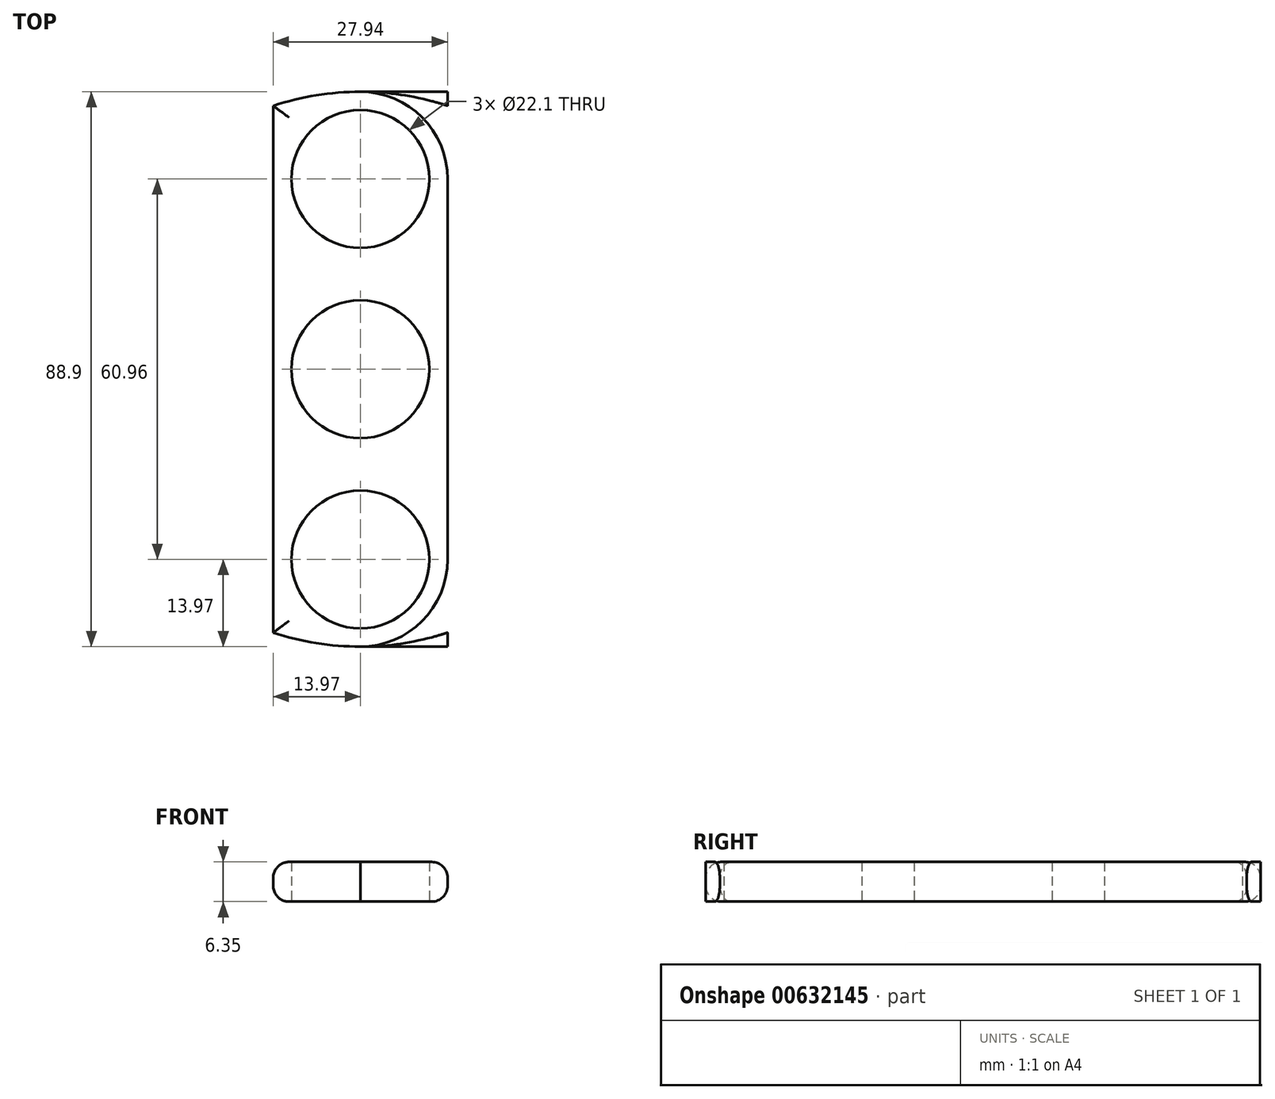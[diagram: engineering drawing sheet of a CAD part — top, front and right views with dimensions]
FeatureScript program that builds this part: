
annotation { "Feature Type Name" : "Feature", "Feature Type Description" : "" }
export const myFeature = defineFeature(function(context is Context, id is Id, definition is map)
    precondition{}
    {
        {
            var Q0;
            Q0=qCreatedBy(makeId("Top.planeOp"),FACE);
            var sketch = newSketch(context, id + "F0", { "sketchPlane" : qUnion([Q0])});
            skCircle(sketch, "E0", {"center": v(0, 0) * mm, "radius": 44.45 * mm});
            skCircle(sketch, "E1", {"center": v(0, 0) * mm, "radius": 11.05 * mm});
            skLineSegment(sketch, "E2", {"start": v(0, 0) * mm, "end": v(0, 30.48) * mm});
            skCircle(sketch, "E3", {"center": v(0, 30.48) * mm, "radius": 11.05 * mm});
            skLineSegment(sketch, "E4", {"start": v(0, 0) * mm, "end": v(0, -30.48) * mm});
            skCircle(sketch, "E5", {"center": v(0, -30.48) * mm, "radius": 11.05 * mm});
            skCircle(sketch, "E6", {"center": v(0, 30.48) * mm, "radius": 13.97 * mm});
            skCircle(sketch, "E7", {"center": v(0, 0) * mm, "radius": 13.97 * mm});
            skCircle(sketch, "E8", {"center": v(0, -30.48) * mm, "radius": 13.97 * mm});
            skLineSegment(sketch, "E9", {"start": v(0, 30.48) * mm, "end": v(0, 44.45) * mm});
            skLineSegment(sketch, "E10", {"start": v(0, 44.45) * mm, "end": v(13.97, 44.45) * mm});
            skLineSegment(sketch, "E11", {"start": v(13.97, 44.45) * mm, "end": v(-13.97, 44.45) * mm});
            skPoint(sketch, "E11.endSnap0", {"position": v(6.99, 44.45) * mm});
            skLineSegment(sketch, "E12", {"start": v(0, -30.48) * mm, "end": v(0, -44.45) * mm});
            skLineSegment(sketch, "E13", {"start": v(0, -44.45) * mm, "end": v(-13.97, -44.45) * mm});
            skLineSegment(sketch, "E14", {"start": v(-13.97, -44.45) * mm, "end": v(13.97, -44.45) * mm});
            skLineSegment(sketch, "E15", {"start": v(13.97, -44.45) * mm, "end": v(13.97, 44.45) * mm});
            skLineSegment(sketch, "E16", {"start": v(-13.97, 44.45) * mm, "end": v(-13.97, -44.45) * mm});
            skSolve(sketch);
        }
        {
            var Q0;
            {var subQ1=sQuery(id+"F0.wireOp",EDGE,"E0");var subQ3=sQuery(id+"F0.wireOp",EDGE,"E16");var subQ4=makeQuery(id+"F0.imprint","INTERSECT",VERTEX,{"disambiguationData":[OD(0.0)],"derivedFrom":[subQ1,subQ3]});Q0=makeQuery(id+"F0.imprint","IMPRINT",FACE,{"disambiguationData":[TD([[makeQuery(id+"F0.imprint","IMPRINT",EDGE,{"disambiguationData":[TD([[subQ4,-1.0]])],"derivedFrom":subQ3}),1.0]])]});}
            var Q1;
            {var subQ1=sQuery(id+"F0.wireOp",EDGE,"E0");var subQ3=sQuery(id+"F0.wireOp",EDGE,"E15");var subQ4=makeQuery(id+"F0.imprint","INTERSECT",VERTEX,{"disambiguationData":[OD(0.0)],"derivedFrom":[subQ1,subQ3]});Q1=makeQuery(id+"F0.imprint","IMPRINT",FACE,{"disambiguationData":[TD([[makeQuery(id+"F0.imprint","IMPRINT",EDGE,{"disambiguationData":[TD([[subQ4,1.0]])],"derivedFrom":subQ3}),1.0]])]});}
            var Q2;
            {var subQ0=sQuery(id+"F0.wireOp",EDGE,"E6");var subQ1=sQuery(id+"F0.wireOp",EDGE,"E2");var subQ2=makeQuery(id+"F0.imprint","INTERSECT",VERTEX,{"derivedFrom":[subQ1,subQ0]});Q2=makeQuery(id+"F0.imprint","IMPRINT",FACE,{"disambiguationData":[TD([[makeQuery(id+"F0.imprint","IMPRINT",EDGE,{"disambiguationData":[TD([[subQ2,-1.0]])],"derivedFrom":subQ1}),-1.0]])]});}
            var Q3;
            {var subQ0=sQuery(id+"F0.wireOp",EDGE,"E6");var subQ1=sQuery(id+"F0.wireOp",EDGE,"E2");var subQ2=makeQuery(id+"F0.imprint","INTERSECT",VERTEX,{"derivedFrom":[subQ1,subQ0]});Q3=makeQuery(id+"F0.imprint","IMPRINT",FACE,{"disambiguationData":[TD([[makeQuery(id+"F0.imprint","IMPRINT",EDGE,{"disambiguationData":[TD([[subQ2,-1.0]])],"derivedFrom":subQ1}),1.0]])]});}
            var Q4;
            {var subQ0=sQuery(id+"F0.wireOp",EDGE,"E7");var subQ1=sQuery(id+"F0.wireOp",EDGE,"E2");var subQ2=makeQuery(id+"F0.imprint","INTERSECT",VERTEX,{"derivedFrom":[subQ1,subQ0]});Q4=makeQuery(id+"F0.imprint","IMPRINT",FACE,{"disambiguationData":[TD([[makeQuery(id+"F0.imprint","IMPRINT",EDGE,{"disambiguationData":[TD([[subQ2,-1.0]])],"derivedFrom":subQ1}),1.0]])]});}
            var Q5;
            {var subQ0=sQuery(id+"F0.wireOp",EDGE,"E7");var subQ1=sQuery(id+"F0.wireOp",EDGE,"E2");var subQ2=makeQuery(id+"F0.imprint","INTERSECT",VERTEX,{"derivedFrom":[subQ1,subQ0]});Q5=makeQuery(id+"F0.imprint","IMPRINT",FACE,{"disambiguationData":[TD([[makeQuery(id+"F0.imprint","IMPRINT",EDGE,{"disambiguationData":[TD([[subQ2,-1.0]])],"derivedFrom":subQ1}),-1.0]])]});}
            var Q6;
            {var subQ1=sQuery(id+"F0.wireOp",EDGE,"E2");var subQ5=sQuery(id+"F0.wireOp",EDGE,"E1");var subQ8=makeQuery(id+"F0.imprint","INTERSECT",VERTEX,{"derivedFrom":[subQ5,subQ1]});Q6=makeQuery(id+"F0.imprint","IMPRINT",FACE,{"disambiguationData":[TD([[makeQuery(id+"F0.imprint","IMPRINT",EDGE,{"disambiguationData":[TD([[subQ8,-1.0]])],"derivedFrom":subQ5}),-1.0]])]});}
            var Q7;
            {var subQ1=sQuery(id+"F0.wireOp",EDGE,"E2");var subQ5=sQuery(id+"F0.wireOp",EDGE,"E1");var subQ8=makeQuery(id+"F0.imprint","INTERSECT",VERTEX,{"derivedFrom":[subQ5,subQ1]});Q7=makeQuery(id+"F0.imprint","IMPRINT",FACE,{"disambiguationData":[TD([[makeQuery(id+"F0.imprint","IMPRINT",EDGE,{"disambiguationData":[TD([[subQ8,1.0]])],"derivedFrom":subQ5}),-1.0]])]});}
            var Q8;
            {var subQ0=sQuery(id+"F0.wireOp",EDGE,"E7");var subQ1=sQuery(id+"F0.wireOp",EDGE,"E4");var subQ2=makeQuery(id+"F0.imprint","INTERSECT",VERTEX,{"derivedFrom":[subQ1,subQ0]});Q8=makeQuery(id+"F0.imprint","IMPRINT",FACE,{"disambiguationData":[TD([[makeQuery(id+"F0.imprint","IMPRINT",EDGE,{"disambiguationData":[TD([[subQ2,-1.0]])],"derivedFrom":subQ1}),-1.0]])]});}
            var Q9;
            {var subQ0=sQuery(id+"F0.wireOp",EDGE,"E7");var subQ1=sQuery(id+"F0.wireOp",EDGE,"E4");var subQ2=makeQuery(id+"F0.imprint","INTERSECT",VERTEX,{"derivedFrom":[subQ1,subQ0]});Q9=makeQuery(id+"F0.imprint","IMPRINT",FACE,{"disambiguationData":[TD([[makeQuery(id+"F0.imprint","IMPRINT",EDGE,{"disambiguationData":[TD([[subQ2,-1.0]])],"derivedFrom":subQ1}),1.0]])]});}
            var Q10;
            {var subQ0=sQuery(id+"F0.wireOp",EDGE,"E8");var subQ1=sQuery(id+"F0.wireOp",EDGE,"E4");var subQ2=makeQuery(id+"F0.imprint","INTERSECT",VERTEX,{"derivedFrom":[subQ1,subQ0]});Q10=makeQuery(id+"F0.imprint","IMPRINT",FACE,{"disambiguationData":[TD([[makeQuery(id+"F0.imprint","IMPRINT",EDGE,{"disambiguationData":[TD([[subQ2,-1.0]])],"derivedFrom":subQ1}),1.0]])]});}
            var Q11;
            {var subQ1=sQuery(id+"F0.wireOp",EDGE,"E8");var subQ4=sQuery(id+"F0.wireOp",EDGE,"E4");var subQ5=makeQuery(id+"F0.imprint","INTERSECT",VERTEX,{"derivedFrom":[subQ4,subQ1]});Q11=makeQuery(id+"F0.imprint","IMPRINT",FACE,{"disambiguationData":[TD([[makeQuery(id+"F0.imprint","IMPRINT",EDGE,{"disambiguationData":[TD([[subQ5,-1.0]])],"derivedFrom":subQ4}),-1.0]])]});}
            var Q12;
            {var subQ1=sQuery(id+"F0.wireOp",EDGE,"E0");var subQ3=sQuery(id+"F0.wireOp",EDGE,"E16");var subQ4=makeQuery(id+"F0.imprint","INTERSECT",VERTEX,{"disambiguationData":[OD(1.0)],"derivedFrom":[subQ1,subQ3]});Q12=makeQuery(id+"F0.imprint","IMPRINT",FACE,{"disambiguationData":[TD([[makeQuery(id+"F0.imprint","IMPRINT",EDGE,{"disambiguationData":[TD([[subQ4,1.0]])],"derivedFrom":subQ3}),1.0]])]});}
            var Q13;
            {var subQ1=sQuery(id+"F0.wireOp",EDGE,"E0");var subQ3=sQuery(id+"F0.wireOp",EDGE,"E15");var subQ4=makeQuery(id+"F0.imprint","INTERSECT",VERTEX,{"disambiguationData":[OD(1.0)],"derivedFrom":[subQ1,subQ3]});Q13=makeQuery(id+"F0.imprint","IMPRINT",FACE,{"disambiguationData":[TD([[makeQuery(id+"F0.imprint","IMPRINT",EDGE,{"disambiguationData":[TD([[subQ4,-1.0]])],"derivedFrom":subQ3}),1.0]])]});}
            extrude(context, id + "F1", {"entities" : qUnion([Q0, Q1, Q2, Q3, Q4, Q5, Q6, Q7, Q8, Q9, Q10, Q11, Q12, Q13]), "depth" : 6.35 * mm, "offsetDistance" : 25.4 * mm});
        }
        {
            var Q0;
            {var subQ0=sQuery(id+"F0.wireOp",EDGE,"E0");Q0=makeQuery(id+"F1.opExtrude","CAP_EDGE",EDGE,{"disambiguationData":[OSD([subQ0]),TDD([makeQuery(id+"F0.imprint","IMPRINT",EDGE,{"disambiguationData":[TD([[makeQuery(id+"F0.imprint","INTERSECT",VERTEX,{"disambiguationData":[OD(1.0)],"derivedFrom":[subQ0,sQuery(id+"F0.wireOp",EDGE,"E16")]}),-1.0]])],"derivedFrom":subQ0}),makeQuery(id+"F0.imprint","IMPRINT",EDGE,{"disambiguationData":[TD([[makeQuery(id+"F0.imprint","INTERSECT",VERTEX,{"disambiguationData":[OD(1.0)],"derivedFrom":[subQ0,sQuery(id+"F0.wireOp",EDGE,"E15")]}),1.0]])],"derivedFrom":subQ0})])],"isStart":false});}
            var Q1;
            {var subQ0=sQuery(id+"F0.wireOp",EDGE,"E0");Q1=makeQuery(id+"F1.opExtrude","CAP_EDGE",EDGE,{"disambiguationData":[OSD([subQ0]),TDD([makeQuery(id+"F0.imprint","IMPRINT",EDGE,{"disambiguationData":[TD([[makeQuery(id+"F0.imprint","INTERSECT",VERTEX,{"disambiguationData":[OD(0.0)],"derivedFrom":[subQ0,sQuery(id+"F0.wireOp",EDGE,"E15")]}),-1.0]])],"derivedFrom":subQ0}),makeQuery(id+"F0.imprint","IMPRINT",EDGE,{"disambiguationData":[TD([[makeQuery(id+"F0.imprint","INTERSECT",VERTEX,{"disambiguationData":[OD(0.0)],"derivedFrom":[subQ0,sQuery(id+"F0.wireOp",EDGE,"E16")]}),1.0]])],"derivedFrom":subQ0})])],"isStart":false});}
            var Q2;
            Q2=makeQuery(id+"F1.opExtrude","CAP_EDGE",EDGE,{"disambiguationData":[OSD([sQuery(id+"F0.wireOp",EDGE,"E15")])],"isStart":false});
            var Q3;
            Q3=makeQuery(id+"F1.opExtrude","CAP_EDGE",EDGE,{"disambiguationData":[OSD([sQuery(id+"F0.wireOp",EDGE,"E16")])],"isStart":false});
            var Q4;
            Q4=makeQuery(id+"F1.opExtrude","CAP_EDGE",EDGE,{"disambiguationData":[OSD([sQuery(id+"F0.wireOp",EDGE,"E15")])],"isStart":true});
            var Q5;
            Q5=makeQuery(id+"F1.opExtrude","CAP_EDGE",EDGE,{"disambiguationData":[OSD([sQuery(id+"F0.wireOp",EDGE,"E16")])],"isStart":true});
            var Q6;
            {var subQ0=sQuery(id+"F0.wireOp",EDGE,"E0");Q6=makeQuery(id+"F1.opExtrude","CAP_EDGE",EDGE,{"disambiguationData":[OSD([subQ0]),TDD([makeQuery(id+"F0.imprint","IMPRINT",EDGE,{"disambiguationData":[TD([[makeQuery(id+"F0.imprint","INTERSECT",VERTEX,{"disambiguationData":[OD(1.0)],"derivedFrom":[subQ0,sQuery(id+"F0.wireOp",EDGE,"E16")]}),-1.0]])],"derivedFrom":subQ0}),makeQuery(id+"F0.imprint","IMPRINT",EDGE,{"disambiguationData":[TD([[makeQuery(id+"F0.imprint","INTERSECT",VERTEX,{"disambiguationData":[OD(1.0)],"derivedFrom":[subQ0,sQuery(id+"F0.wireOp",EDGE,"E15")]}),1.0]])],"derivedFrom":subQ0})])],"isStart":true});}
            var Q7;
            {var subQ0=sQuery(id+"F0.wireOp",EDGE,"E0");Q7=makeQuery(id+"F1.opExtrude","CAP_EDGE",EDGE,{"disambiguationData":[OSD([subQ0]),TDD([makeQuery(id+"F0.imprint","IMPRINT",EDGE,{"disambiguationData":[TD([[makeQuery(id+"F0.imprint","INTERSECT",VERTEX,{"disambiguationData":[OD(0.0)],"derivedFrom":[subQ0,sQuery(id+"F0.wireOp",EDGE,"E15")]}),-1.0]])],"derivedFrom":subQ0}),makeQuery(id+"F0.imprint","IMPRINT",EDGE,{"disambiguationData":[TD([[makeQuery(id+"F0.imprint","INTERSECT",VERTEX,{"disambiguationData":[OD(0.0)],"derivedFrom":[subQ0,sQuery(id+"F0.wireOp",EDGE,"E16")]}),1.0]])],"derivedFrom":subQ0})])],"isStart":true});}
            fillet(context, id + "F2", {"entities" : qUnion([Q0, Q1, Q2, Q3, Q4, Q5, Q6, Q7]), "radius" : 2.54 * mm, "tangentPropagation" : true, "allowEdgeOverflow" : false});
        }
    });
